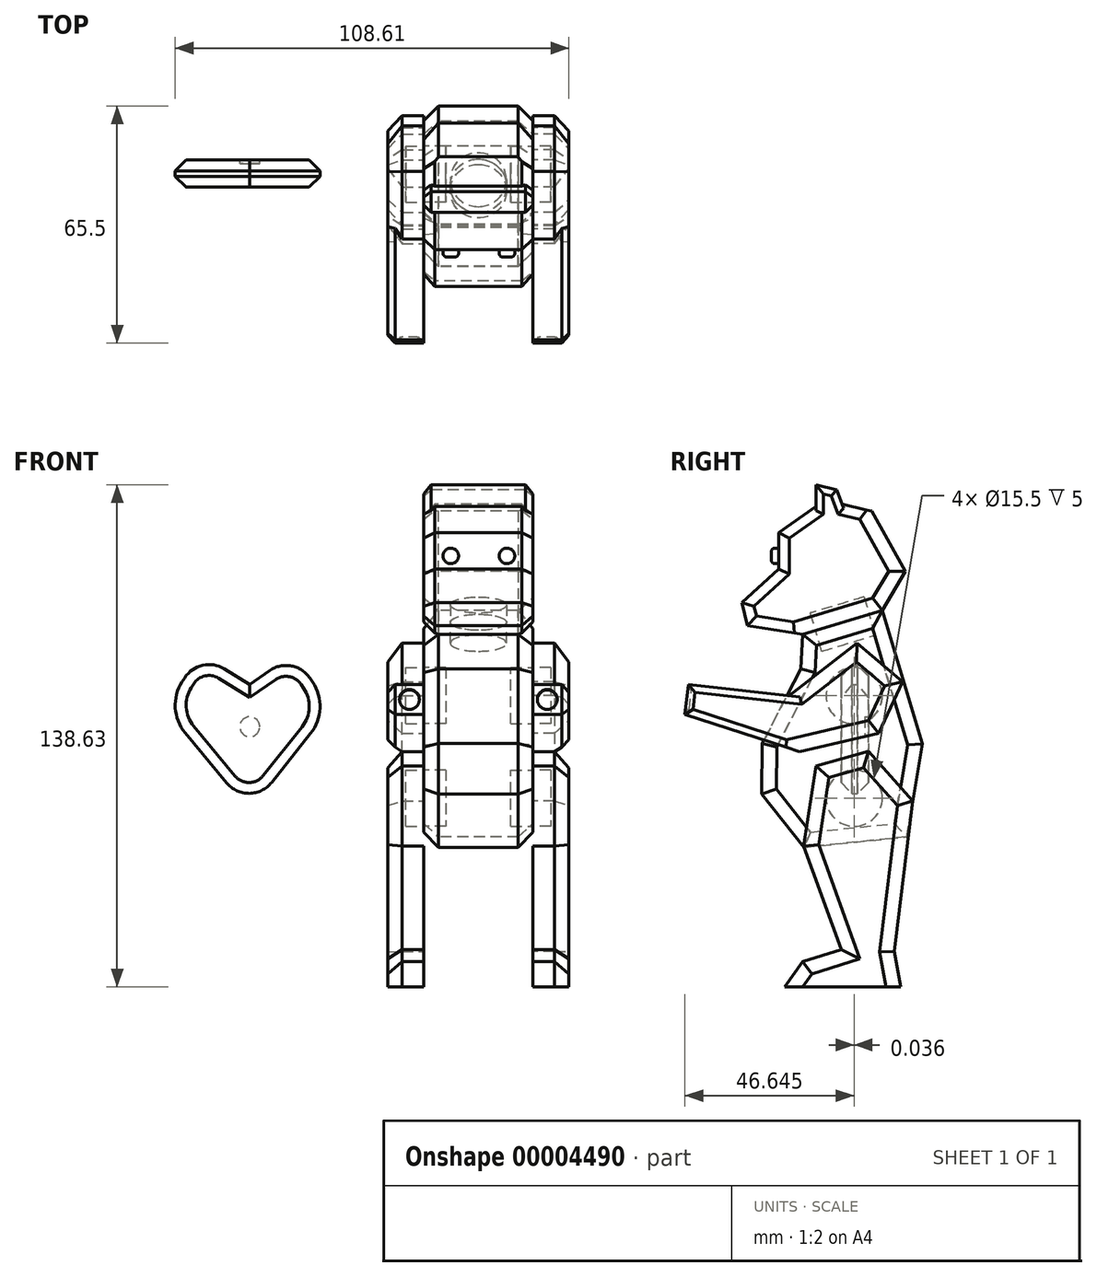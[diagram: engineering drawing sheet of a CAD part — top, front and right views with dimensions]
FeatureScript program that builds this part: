
annotation { "Feature Type Name" : "Feature", "Feature Type Description" : "" }
export const myFeature = defineFeature(function(context is Context, id is Id, definition is map)
    precondition{}
    {
        {
            var Q0;
            Q0=qCreatedBy(makeId("Right.planeOp"),FACE);
            var sketch = newSketch(context, id + "F0", { "sketchPlane" : qUnion([Q0])});
            skLineSegment(sketch, "E0", {"start": v(8.96, -80.35) * mm, "end": v(-23.04, -80.35) * mm});
            skLineSegment(sketch, "E1", {"start": v(-23.04, -80.35) * mm, "end": v(-18.1, -73.4) * mm});
            skLineSegment(sketch, "E2", {"start": v(-18.1, -73.4) * mm, "end": v(-7.52, -70.04) * mm});
            skLineSegment(sketch, "E3", {"start": v(-7.52, -70.04) * mm, "end": v(-17.86, -41.48) * mm});
            skLineSegment(sketch, "E4", {"start": v(-17.86, -41.48) * mm, "end": v(-14.49, -19.35) * mm});
            skLineSegment(sketch, "E5", {"start": v(-14.49, -19.35) * mm, "end": v(0, -15.35) * mm});
            skLineSegment(sketch, "E6", {"start": v(0, -15.35) * mm, "end": v(12.2, -28.97) * mm});
            skLineSegment(sketch, "E7", {"start": v(12.2, -28.97) * mm, "end": v(7.15, -70.52) * mm});
            skLineSegment(sketch, "E8", {"start": v(7.15, -70.52) * mm, "end": v(8.96, -80.35) * mm});
            skCircle(sketch, "E9", {"center": v(-3.9, -28.25) * mm, "radius": 7.75 * mm});
            skSolve(sketch);
        }
        {
            var Q0;
            Q0=qCreatedBy(makeId("Right.planeOp"),FACE);
            var sketch = newSketch(context, id + "F1", { "sketchPlane" : qUnion([Q0])});
            skLineSegment(sketch, "E10", {"start": v(10.62, -38.93) * mm, "end": v(14.91, -13.21) * mm});
            skLineSegment(sketch, "E11", {"start": v(14.91, -13.21) * mm, "end": v(3.82, 23.58) * mm});
            skLineSegment(sketch, "E12", {"start": v(3.82, 23.58) * mm, "end": v(-18.18, 16.97) * mm});
            skLineSegment(sketch, "E13", {"start": v(-18.18, 16.97) * mm, "end": v(-18.65, 7.45) * mm});
            skLineSegment(sketch, "E14", {"start": v(-18.65, 7.45) * mm, "end": v(-29.28, -13.16) * mm});
            skLineSegment(sketch, "E15", {"start": v(-29.28, -13.16) * mm, "end": v(-29.44, -27.12) * mm});
            skLineSegment(sketch, "E16", {"start": v(-29.44, -27.12) * mm, "end": v(-17.76, -41.8) * mm});
            skLineSegment(sketch, "E17", {"start": v(-17.76, -41.8) * mm, "end": v(10.62, -38.93) * mm});
            skLineSegment(sketch, "E18", {"start": v(-3.9, -28.25) * mm, "end": v(-3.9, 9.99) * mm, "construction": true});
            skCircle(sketch, "E19", {"center": v(-3.9, 0) * mm, "radius": 7.75 * mm});
            skCircle(sketch, "E20", {"center": v(-3.9, -28.25) * mm, "radius": 7.75 * mm});
            skSolve(sketch);
        }
        {
            var Q0;
            Q0=qCreatedBy(makeId("Right.planeOp"),FACE);
            var sketch = newSketch(context, id + "F2", { "sketchPlane" : qUnion([Q0])});
            skLineSegment(sketch, "E21", {"start": v(-3.18, 14.54) * mm, "end": v(9.44, 3.85) * mm});
            skLineSegment(sketch, "E22", {"start": v(9.44, 3.85) * mm, "end": v(2.83, -10.31) * mm});
            skLineSegment(sketch, "E23", {"start": v(2.83, -10.31) * mm, "end": v(-19.03, -15.4) * mm});
            skLineSegment(sketch, "E24", {"start": v(-19.03, -15.4) * mm, "end": v(-50.59, -5.17) * mm});
            skLineSegment(sketch, "E25", {"start": v(-50.59, -5.17) * mm, "end": v(-49.66, 3.12) * mm});
            skLineSegment(sketch, "E26", {"start": v(-49.66, 3.12) * mm, "end": v(-21.8, 0) * mm});
            skLineSegment(sketch, "E27", {"start": v(-21.8, 0) * mm, "end": v(-3.18, 14.54) * mm});
            skCircle(sketch, "E28", {"center": v(-3.94, 0) * mm, "radius": 7.75 * mm});
            skSolve(sketch);
        }
        {
            var Q0;
            Q0=qCreatedBy(makeId("Right.planeOp"),FACE);
            var sketch = newSketch(context, id + "F3", { "sketchPlane" : qUnion([Q0])});
            skLineSegment(sketch, "E29", {"start": v(-18.18, 16.97) * mm, "end": v(3.82, 23.58) * mm});
            skLineSegment(sketch, "E30", {"start": v(3.82, 23.58) * mm, "end": v(10.17, 34.3) * mm});
            skLineSegment(sketch, "E31", {"start": v(10.17, 34.3) * mm, "end": v(0.9, 50.93) * mm});
            skLineSegment(sketch, "E32", {"start": v(0.9, 50.93) * mm, "end": v(-7.26, 52.9) * mm});
            skLineSegment(sketch, "E33", {"start": v(-7.26, 52.9) * mm, "end": v(-8.76, 56.87) * mm});
            skLineSegment(sketch, "E34", {"start": v(-8.76, 56.87) * mm, "end": v(-14.44, 58.28) * mm});
            skLineSegment(sketch, "E35", {"start": v(-14.44, 58.28) * mm, "end": v(-14.44, 52.32) * mm});
            skLineSegment(sketch, "E36", {"start": v(-14.44, 52.32) * mm, "end": v(-24.78, 45) * mm});
            skLineSegment(sketch, "E37", {"start": v(-24.78, 45) * mm, "end": v(-24.78, 34.93) * mm});
            skLineSegment(sketch, "E38", {"start": v(-24.78, 34.93) * mm, "end": v(-34.87, 25.75) * mm});
            skLineSegment(sketch, "E39", {"start": v(-34.87, 25.75) * mm, "end": v(-33.35, 19.37) * mm});
            skLineSegment(sketch, "E40", {"start": v(-33.35, 19.37) * mm, "end": v(-18.18, 16.97) * mm});
            skSolve(sketch);
        }
        {
            var Q0;
            Q0=makeQuery(id+"F1.imprint","IMPRINT",FACE,{"disambiguationData":[TD([[makeQuery(id+"F1.imprint","IMPRINT",EDGE,{"derivedFrom":sQuery(id+"F1.wireOp",EDGE,"E10")}),1.0]])]});
            var Q1;
            Q1=makeQuery(id+"F1.imprint","IMPRINT",FACE,{"disambiguationData":[TD([[makeQuery(id+"F1.imprint","IMPRINT",EDGE,{"derivedFrom":sQuery(id+"F1.wireOp",EDGE,"E20")}),1.0]])]});
            var Q2;
            Q2=makeQuery(id+"F1.imprint","IMPRINT",FACE,{"disambiguationData":[TD([[makeQuery(id+"F1.imprint","IMPRINT",EDGE,{"derivedFrom":sQuery(id+"F1.wireOp",EDGE,"E19")}),1.0]])]});
            extrude(context, id + "F4", {"entities" : qUnion([Q0, Q1, Q2]), "depth" : 30 * mm});
        }
        {
            var Q0;
            Q0=makeQuery(id+"F4.opExtrude","CAP_EDGE",EDGE,{"disambiguationData":[OSD([sQuery(id+"F1.wireOp",EDGE,"E15")])],"isStart":false});
            var Q1;
            Q1=makeQuery(id+"F4.opExtrude","CAP_EDGE",EDGE,{"disambiguationData":[OSD([sQuery(id+"F1.wireOp",EDGE,"E14")])],"isStart":false});
            var Q2;
            Q2=makeQuery(id+"F4.opExtrude","CAP_EDGE",EDGE,{"disambiguationData":[OSD([sQuery(id+"F1.wireOp",EDGE,"E13")])],"isStart":false});
            var Q3;
            Q3=makeQuery(id+"F4.opExtrude","CAP_EDGE",EDGE,{"disambiguationData":[OSD([sQuery(id+"F1.wireOp",EDGE,"E12")])],"isStart":false});
            var Q4;
            Q4=makeQuery(id+"F4.opExtrude","CAP_FACE",FACE,{"disambiguationData":[OSD([sQuery(id+"F1.wireOp",EDGE,"E10"),sQuery(id+"F1.wireOp",EDGE,"E11"),sQuery(id+"F1.wireOp",EDGE,"E12"),sQuery(id+"F1.wireOp",EDGE,"E13"),sQuery(id+"F1.wireOp",EDGE,"E14"),sQuery(id+"F1.wireOp",EDGE,"E15"),sQuery(id+"F1.wireOp",EDGE,"E16"),sQuery(id+"F1.wireOp",EDGE,"E17")])],"isStart":false});
            var Q5;
            Q5=makeQuery(id+"F4.opExtrude","CAP_FACE",FACE,{"disambiguationData":[OSD([sQuery(id+"F1.wireOp",EDGE,"E10"),sQuery(id+"F1.wireOp",EDGE,"E11"),sQuery(id+"F1.wireOp",EDGE,"E12"),sQuery(id+"F1.wireOp",EDGE,"E13"),sQuery(id+"F1.wireOp",EDGE,"E14"),sQuery(id+"F1.wireOp",EDGE,"E15"),sQuery(id+"F1.wireOp",EDGE,"E16"),sQuery(id+"F1.wireOp",EDGE,"E17")])],"isStart":true});
            chamfer(context, id + "F5", {"entities" : qUnion([Q0, Q1, Q2, Q3, Q4, Q5]), "width" : 4 * mm, "tangentPropagation" : true});
        }
        {
            var Q0;
            Q0=makeQuery(id+"F4.opExtrude","CAP_FACE",FACE,{"disambiguationData":[OSD([sQuery(id+"F1.wireOp",EDGE,"E10"),sQuery(id+"F1.wireOp",EDGE,"E11"),sQuery(id+"F1.wireOp",EDGE,"E12"),sQuery(id+"F1.wireOp",EDGE,"E13"),sQuery(id+"F1.wireOp",EDGE,"E14"),sQuery(id+"F1.wireOp",EDGE,"E15"),sQuery(id+"F1.wireOp",EDGE,"E16"),sQuery(id+"F1.wireOp",EDGE,"E17")])],"isStart":false});
            var sketch = newSketch(context, id + "F6", { "sketchPlane" : qUnion([Q0])});
            skCircle(sketch, "E41", {"center": v(-3.9, 0) * mm, "radius": 7.75 * mm});
            skCircle(sketch, "E42", {"center": v(-3.9, -28.25) * mm, "radius": 7.75 * mm});
            skSolve(sketch);
        }
        {
            var Q0;
            Q0=makeQuery(id+"F6.imprint","IMPRINT",FACE,{"disambiguationData":[TD([[makeQuery(id+"F6.imprint","IMPRINT",EDGE,{"derivedFrom":sQuery(id+"F6.wireOp",EDGE,"E41")}),1.0]])]});
            var Q1;
            Q1=makeQuery(id+"F6.imprint","IMPRINT",FACE,{"disambiguationData":[TD([[makeQuery(id+"F6.imprint","IMPRINT",EDGE,{"derivedFrom":sQuery(id+"F6.wireOp",EDGE,"E42")}),1.0]])]});
            extrude(context, id + "F7", {"entities" : qUnion([Q0, Q1]), "operationType" : NewBodyOperationType.REMOVE, "oppositeDirection" : true, "depth" : 6 * mm});
        }
        {
            var Q0;
            Q0=makeQuery(id+"F4.opExtrude","CAP_FACE",FACE,{"disambiguationData":[OSD([sQuery(id+"F1.wireOp",EDGE,"E10"),sQuery(id+"F1.wireOp",EDGE,"E11"),sQuery(id+"F1.wireOp",EDGE,"E12"),sQuery(id+"F1.wireOp",EDGE,"E13"),sQuery(id+"F1.wireOp",EDGE,"E14"),sQuery(id+"F1.wireOp",EDGE,"E15"),sQuery(id+"F1.wireOp",EDGE,"E16"),sQuery(id+"F1.wireOp",EDGE,"E17")])],"isStart":false});
            var Q1;
            Q1=makeQuery(id+"F4.opExtrude","CAP_FACE",FACE,{"disambiguationData":[OSD([sQuery(id+"F1.wireOp",EDGE,"E10"),sQuery(id+"F1.wireOp",EDGE,"E11"),sQuery(id+"F1.wireOp",EDGE,"E12"),sQuery(id+"F1.wireOp",EDGE,"E13"),sQuery(id+"F1.wireOp",EDGE,"E14"),sQuery(id+"F1.wireOp",EDGE,"E15"),sQuery(id+"F1.wireOp",EDGE,"E16"),sQuery(id+"F1.wireOp",EDGE,"E17")])],"isStart":true});
            cPlane(context, id + "F8", {"entities" : qUnion([Q0, Q1]), "cplaneType" : CPlaneType.MID_PLANE, "offset" : 150 * mm, "width" : 150 * mm, "height" : 150 * mm});
        }
        {
            var Q0;
            Q0=makeQuery(id+"F4.opExtrude","CAP_FACE",FACE,{"disambiguationData":[OSD([sQuery(id+"F1.wireOp",EDGE,"E10"),sQuery(id+"F1.wireOp",EDGE,"E11"),sQuery(id+"F1.wireOp",EDGE,"E12"),sQuery(id+"F1.wireOp",EDGE,"E13"),sQuery(id+"F1.wireOp",EDGE,"E14"),sQuery(id+"F1.wireOp",EDGE,"E15"),sQuery(id+"F1.wireOp",EDGE,"E16"),sQuery(id+"F1.wireOp",EDGE,"E17")])],"isStart":true});
            var sketch = newSketch(context, id + "F9", { "sketchPlane" : qUnion([Q0])});
            skCircle(sketch, "E43", {"center": v(3.9, -28.25) * mm, "radius": 7.75 * mm});
            skCircle(sketch, "E44", {"center": v(3.9, 0) * mm, "radius": 7.75 * mm});
            skSolve(sketch);
        }
        {
            var Q0;
            Q0=makeQuery(id+"F9.imprint","IMPRINT",FACE,{"disambiguationData":[TD([[makeQuery(id+"F9.imprint","IMPRINT",EDGE,{"derivedFrom":sQuery(id+"F9.wireOp",EDGE,"E44")}),1.0]])]});
            var Q1;
            Q1=makeQuery(id+"F9.imprint","IMPRINT",FACE,{"disambiguationData":[TD([[makeQuery(id+"F9.imprint","IMPRINT",EDGE,{"derivedFrom":sQuery(id+"F9.wireOp",EDGE,"E43")}),1.0]])]});
            extrude(context, id + "F10", {"entities" : qUnion([Q0, Q1]), "operationType" : NewBodyOperationType.REMOVE, "oppositeDirection" : true, "depth" : 6 * mm});
        }
        {
            var Q0;
            Q0=makeQuery(id+"F4.opExtrude","SWEPT_FACE",FACE,{"disambiguationData":[OSD([sQuery(id+"F1.wireOp",EDGE,"E12")])]});
            var sketch = newSketch(context, id + "F11", { "sketchPlane" : qUnion([Q0])});
            skLineSegment(sketch, "E45", {"start": v(4, 10.45) * mm, "end": v(26, -12.53) * mm, "construction": true});
            skLineSegment(sketch, "E46", {"start": v(4, -12.53) * mm, "end": v(26, 10.45) * mm, "construction": true});
            skCircle(sketch, "E47", {"center": v(15, -1.04) * mm, "radius": 7.75 * mm});
            skSolve(sketch);
        }
        {
            var Q0;
            Q0=makeQuery(id+"F11.imprint","IMPRINT",FACE,{"disambiguationData":[TD([[makeQuery(id+"F11.imprint","IMPRINT",EDGE,{"derivedFrom":sQuery(id+"F11.wireOp",EDGE,"E47")}),1.0]])]});
            extrude(context, id + "F12", {"entities" : qUnion([Q0]), "operationType" : NewBodyOperationType.REMOVE, "oppositeDirection" : true, "depth" : 6 * mm});
        }
        {
            var Q0;
            Q0=makeQuery(id+"F3.imprint","IMPRINT",FACE,{"disambiguationData":[TD([[makeQuery(id+"F3.imprint","IMPRINT",EDGE,{"derivedFrom":sQuery(id+"F3.wireOp",EDGE,"E29")}),1.0]])]});
            extrude(context, id + "F13", {"entities" : qUnion([Q0]), "depth" : 30 * mm});
        }
        {
            var Q0;
            Q0=makeQuery(id+"F13.opExtrude","CAP_EDGE",EDGE,{"disambiguationData":[OSD([sQuery(id+"F3.wireOp",EDGE,"E29")])],"isStart":false});
            var Q1;
            Q1=makeQuery(id+"F13.opExtrude","CAP_EDGE",EDGE,{"disambiguationData":[OSD([sQuery(id+"F3.wireOp",EDGE,"E29")])],"isStart":true});
            var Q2;
            Q2=makeQuery(id+"F13.opExtrude","CAP_EDGE",EDGE,{"disambiguationData":[OSD([sQuery(id+"F3.wireOp",EDGE,"E30")])],"isStart":false});
            var Q3;
            Q3=makeQuery(id+"F13.opExtrude","CAP_EDGE",EDGE,{"disambiguationData":[OSD([sQuery(id+"F3.wireOp",EDGE,"E31")])],"isStart":false});
            var Q4;
            Q4=makeQuery(id+"F13.opExtrude","CAP_EDGE",EDGE,{"disambiguationData":[OSD([sQuery(id+"F3.wireOp",EDGE,"E30")])],"isStart":true});
            var Q5;
            Q5=makeQuery(id+"F13.opExtrude","CAP_EDGE",EDGE,{"disambiguationData":[OSD([sQuery(id+"F3.wireOp",EDGE,"E31")])],"isStart":true});
            chamfer(context, id + "F14", {"entities" : qUnion([Q0, Q1, Q2, Q3, Q4, Q5]), "width" : 4 * mm, "tangentPropagation" : true});
        }
        {
            var Q0;
            Q0=makeQuery(id+"F13.opExtrude","CAP_EDGE",EDGE,{"disambiguationData":[OSD([sQuery(id+"F3.wireOp",EDGE,"E40")])],"isStart":false});
            var Q1;
            Q1=makeQuery(id+"F13.opExtrude","CAP_EDGE",EDGE,{"disambiguationData":[OSD([sQuery(id+"F3.wireOp",EDGE,"E39")])],"isStart":false});
            var Q2;
            Q2=makeQuery(id+"F13.opExtrude","CAP_EDGE",EDGE,{"disambiguationData":[OSD([sQuery(id+"F3.wireOp",EDGE,"E38")])],"isStart":false});
            var Q3;
            Q3=makeQuery(id+"F13.opExtrude","CAP_EDGE",EDGE,{"disambiguationData":[OSD([sQuery(id+"F3.wireOp",EDGE,"E37")])],"isStart":false});
            var Q4;
            Q4=makeQuery(id+"F13.opExtrude","CAP_EDGE",EDGE,{"disambiguationData":[OSD([sQuery(id+"F3.wireOp",EDGE,"E36")])],"isStart":false});
            var Q5;
            Q5=makeQuery(id+"F13.opExtrude","CAP_EDGE",EDGE,{"disambiguationData":[OSD([sQuery(id+"F3.wireOp",EDGE,"E32")])],"isStart":false});
            var Q6;
            Q6=makeQuery(id+"F13.opExtrude","CAP_EDGE",EDGE,{"disambiguationData":[OSD([sQuery(id+"F3.wireOp",EDGE,"E32")])],"isStart":true});
            var Q7;
            Q7=makeQuery(id+"F13.opExtrude","CAP_EDGE",EDGE,{"disambiguationData":[OSD([sQuery(id+"F3.wireOp",EDGE,"E36")])],"isStart":true});
            var Q8;
            Q8=makeQuery(id+"F13.opExtrude","CAP_EDGE",EDGE,{"disambiguationData":[OSD([sQuery(id+"F3.wireOp",EDGE,"E37")])],"isStart":true});
            var Q9;
            Q9=makeQuery(id+"F13.opExtrude","CAP_EDGE",EDGE,{"disambiguationData":[OSD([sQuery(id+"F3.wireOp",EDGE,"E38")])],"isStart":true});
            var Q10;
            Q10=makeQuery(id+"F13.opExtrude","CAP_EDGE",EDGE,{"disambiguationData":[OSD([sQuery(id+"F3.wireOp",EDGE,"E39")])],"isStart":true});
            var Q11;
            Q11=makeQuery(id+"F13.opExtrude","CAP_EDGE",EDGE,{"disambiguationData":[OSD([sQuery(id+"F3.wireOp",EDGE,"E40")])],"isStart":true});
            chamfer(context, id + "F15", {"entities" : qUnion([Q0, Q1, Q2, Q3, Q4, Q5, Q6, Q7, Q8, Q9, Q10, Q11]), "width" : 3 * mm, "tangentPropagation" : true});
        }
        {
            var Q0;
            Q0=makeQuery(id+"F13.opExtrude","CAP_EDGE",EDGE,{"disambiguationData":[OSD([sQuery(id+"F3.wireOp",EDGE,"E35")])],"isStart":false});
            var Q1;
            Q1=makeQuery(id+"F13.opExtrude","CAP_EDGE",EDGE,{"disambiguationData":[OSD([sQuery(id+"F3.wireOp",EDGE,"E33")])],"isStart":false});
            var Q2;
            Q2=makeQuery(id+"F13.opExtrude","CAP_EDGE",EDGE,{"disambiguationData":[OSD([sQuery(id+"F3.wireOp",EDGE,"E34")])],"isStart":false});
            var Q3;
            Q3=makeQuery(id+"F13.opExtrude","CAP_EDGE",EDGE,{"disambiguationData":[OSD([sQuery(id+"F3.wireOp",EDGE,"E33")])],"isStart":true});
            var Q4;
            Q4=makeQuery(id+"F13.opExtrude","CAP_EDGE",EDGE,{"disambiguationData":[OSD([sQuery(id+"F3.wireOp",EDGE,"E35")])],"isStart":true});
            var Q5;
            Q5=makeQuery(id+"F13.opExtrude","CAP_EDGE",EDGE,{"disambiguationData":[OSD([sQuery(id+"F3.wireOp",EDGE,"E34")])],"isStart":true});
            chamfer(context, id + "F16", {"entities" : qUnion([Q0, Q1, Q2, Q3, Q4, Q5]), "width" : 2 * mm, "tangentPropagation" : true});
        }
        {
            var Q0;
            Q0=makeQuery(id+"F2.imprint","IMPRINT",FACE,{"disambiguationData":[TD([[makeQuery(id+"F2.imprint","IMPRINT",EDGE,{"derivedFrom":sQuery(id+"F2.wireOp",EDGE,"E21")}),-1.0]])]});
            var Q1;
            Q1=makeQuery(id+"F2.imprint","IMPRINT",FACE,{"disambiguationData":[TD([[makeQuery(id+"F2.imprint","IMPRINT",EDGE,{"derivedFrom":sQuery(id+"F2.wireOp",EDGE,"E28")}),1.0]])]});
            extrude(context, id + "F17", {"entities" : qUnion([Q0, Q1]), "oppositeDirection" : true, "depth" : 10 * mm});
        }
        {
            var Q0;
            Q0=makeQuery(id+"F13.opExtrude","SWEPT_FACE",FACE,{"disambiguationData":[OSD([sQuery(id+"F3.wireOp",EDGE,"E29")])]});
            var sketch = newSketch(context, id + "F18", { "sketchPlane" : qUnion([Q0])});
            skLineSegment(sketch, "E48", {"start": v(26, -10.44) * mm, "end": v(4, 12.52) * mm, "construction": true});
            skLineSegment(sketch, "E49", {"start": v(26, 12.52) * mm, "end": v(4, -10.44) * mm, "construction": true});
            skCircle(sketch, "E50", {"center": v(15, 1.04) * mm, "radius": 7.75 * mm});
            skSolve(sketch);
        }
        {
            var Q0;
            Q0=makeQuery(id+"F18.imprint","IMPRINT",FACE,{"disambiguationData":[TD([[makeQuery(id+"F18.imprint","IMPRINT",EDGE,{"derivedFrom":sQuery(id+"F18.wireOp",EDGE,"E50")}),1.0]])]});
            extrude(context, id + "F19", {"entities" : qUnion([Q0]), "operationType" : NewBodyOperationType.REMOVE, "oppositeDirection" : true, "depth" : 5 * mm});
        }
        {
            var Q0;
            Q0=makeQuery(id+"F2.imprint","IMPRINT",FACE,{"disambiguationData":[TD([[makeQuery(id+"F2.imprint","IMPRINT",EDGE,{"derivedFrom":sQuery(id+"F2.wireOp",EDGE,"E21")}),-1.0]])]});
            var sketch = newSketch(context, id + "F20", { "sketchPlane" : qUnion([Q0])});
            skCircle(sketch, "E51", {"center": v(-3.94, 0) * mm, "radius": 7.75 * mm});
            skSolve(sketch);
        }
        {
            var Q0;
            Q0=makeQuery(id+"F17.opExtrude","SWEPT_BODY",BODY,{"disambiguationData":[OSD([sQuery(id+"F2.wireOp",EDGE,"E21"),sQuery(id+"F2.wireOp",EDGE,"E22"),sQuery(id+"F2.wireOp",EDGE,"E23"),sQuery(id+"F2.wireOp",EDGE,"E24"),sQuery(id+"F2.wireOp",EDGE,"E25"),sQuery(id+"F2.wireOp",EDGE,"E26"),sQuery(id+"F2.wireOp",EDGE,"E27")])]});
            var Q1;
            Q1=qCreatedBy(id+"F8.planeOp",FACE);
            mirror(context, id + "F21", {"entities" : qUnion([Q0]), "mirrorPlane" : qUnion([Q1])});
        }
        {
            var Q0;
            Q0=makeQuery(id+"F0.imprint","IMPRINT",FACE,{"disambiguationData":[TD([[makeQuery(id+"F0.imprint","IMPRINT",EDGE,{"derivedFrom":sQuery(id+"F0.wireOp",EDGE,"E0")}),-1.0]])]});
            var Q1;
            Q1=makeQuery(id+"F0.imprint","IMPRINT",FACE,{"disambiguationData":[TD([[makeQuery(id+"F0.imprint","IMPRINT",EDGE,{"derivedFrom":sQuery(id+"F0.wireOp",EDGE,"E9")}),1.0]])]});
            extrude(context, id + "F22", {"entities" : qUnion([Q0, Q1]), "oppositeDirection" : true, "depth" : 10 * mm});
        }
        {
            var Q0;
            Q0=makeQuery(id+"F22.opExtrude","SWEPT_BODY",BODY,{"disambiguationData":[OSD([sQuery(id+"F0.wireOp",EDGE,"E0"),sQuery(id+"F0.wireOp",EDGE,"E1"),sQuery(id+"F0.wireOp",EDGE,"E2"),sQuery(id+"F0.wireOp",EDGE,"E3"),sQuery(id+"F0.wireOp",EDGE,"E4"),sQuery(id+"F0.wireOp",EDGE,"E5"),sQuery(id+"F0.wireOp",EDGE,"E6"),sQuery(id+"F0.wireOp",EDGE,"E7"),sQuery(id+"F0.wireOp",EDGE,"E8")])]});
            var Q1;
            Q1=qCreatedBy(id+"F8.planeOp",FACE);
            mirror(context, id + "F23", {"entities" : qUnion([Q0]), "mirrorPlane" : qUnion([Q1])});
        }
        {
            var Q0;
            Q0=makeQuery(id+"F22.opExtrude","CAP_EDGE",EDGE,{"disambiguationData":[OSD([sQuery(id+"F0.wireOp",EDGE,"E6")])],"isStart":false});
            var Q1;
            Q1=makeQuery(id+"F22.opExtrude","CAP_EDGE",EDGE,{"disambiguationData":[OSD([sQuery(id+"F0.wireOp",EDGE,"E5")])],"isStart":false});
            var Q2;
            Q2=makeQuery(id+"F22.opExtrude","CAP_EDGE",EDGE,{"disambiguationData":[OSD([sQuery(id+"F0.wireOp",EDGE,"E4")])],"isStart":false});
            var Q3;
            Q3=makeQuery(id+"F22.opExtrude","CAP_EDGE",EDGE,{"disambiguationData":[OSD([sQuery(id+"F0.wireOp",EDGE,"E3")])],"isStart":false});
            var Q4;
            Q4=makeQuery(id+"F22.opExtrude","CAP_EDGE",EDGE,{"disambiguationData":[OSD([sQuery(id+"F0.wireOp",EDGE,"E7")])],"isStart":false});
            var Q5;
            Q5=makeQuery(id+"F23.opPattern","COPY",EDGE,{"derivedFrom":makeQuery(id+"F22.opExtrude","CAP_EDGE",EDGE,{"disambiguationData":[OSD([sQuery(id+"F0.wireOp",EDGE,"E5")])],"isStart":false}),"instanceName":"1"});
            var Q6;
            Q6=makeQuery(id+"F23.opPattern","COPY",EDGE,{"derivedFrom":makeQuery(id+"F22.opExtrude","CAP_EDGE",EDGE,{"disambiguationData":[OSD([sQuery(id+"F0.wireOp",EDGE,"E6")])],"isStart":false}),"instanceName":"1"});
            var Q7;
            Q7=makeQuery(id+"F23.opPattern","COPY",EDGE,{"derivedFrom":makeQuery(id+"F22.opExtrude","CAP_EDGE",EDGE,{"disambiguationData":[OSD([sQuery(id+"F0.wireOp",EDGE,"E4")])],"isStart":false}),"instanceName":"1"});
            var Q8;
            Q8=makeQuery(id+"F23.opPattern","COPY",EDGE,{"derivedFrom":makeQuery(id+"F22.opExtrude","CAP_EDGE",EDGE,{"disambiguationData":[OSD([sQuery(id+"F0.wireOp",EDGE,"E3")])],"isStart":false}),"instanceName":"1"});
            var Q9;
            Q9=makeQuery(id+"F23.opPattern","COPY",EDGE,{"derivedFrom":makeQuery(id+"F22.opExtrude","CAP_EDGE",EDGE,{"disambiguationData":[OSD([sQuery(id+"F0.wireOp",EDGE,"E7")])],"isStart":false}),"instanceName":"1"});
            var Q10;
            Q10=makeQuery(id+"F22.opExtrude","CAP_EDGE",EDGE,{"disambiguationData":[OSD([sQuery(id+"F0.wireOp",EDGE,"E8")])],"isStart":false});
            var Q11;
            Q11=makeQuery(id+"F23.opPattern","COPY",EDGE,{"derivedFrom":makeQuery(id+"F22.opExtrude","CAP_EDGE",EDGE,{"disambiguationData":[OSD([sQuery(id+"F0.wireOp",EDGE,"E8")])],"isStart":false}),"instanceName":"1"});
            var Q12;
            Q12=makeQuery(id+"F23.opPattern","COPY",EDGE,{"derivedFrom":makeQuery(id+"F22.opExtrude","CAP_EDGE",EDGE,{"disambiguationData":[OSD([sQuery(id+"F0.wireOp",EDGE,"E2")])],"isStart":false}),"instanceName":"1"});
            var Q13;
            Q13=makeQuery(id+"F23.opPattern","COPY",EDGE,{"derivedFrom":makeQuery(id+"F22.opExtrude","CAP_EDGE",EDGE,{"disambiguationData":[OSD([sQuery(id+"F0.wireOp",EDGE,"E1")])],"isStart":false}),"instanceName":"1"});
            var Q14;
            Q14=makeQuery(id+"F22.opExtrude","CAP_EDGE",EDGE,{"disambiguationData":[OSD([sQuery(id+"F0.wireOp",EDGE,"E2")])],"isStart":false});
            var Q15;
            Q15=makeQuery(id+"F22.opExtrude","CAP_EDGE",EDGE,{"disambiguationData":[OSD([sQuery(id+"F0.wireOp",EDGE,"E1")])],"isStart":false});
            chamfer(context, id + "F24", {"entities" : qUnion([Q0, Q1, Q2, Q3, Q4, Q5, Q6, Q7, Q8, Q9, Q10, Q11, Q12, Q13, Q14, Q15]), "width" : 4 * mm, "tangentPropagation" : true});
        }
        {
            var Q0;
            Q0=makeQuery(id+"F21.opPattern","COPY",EDGE,{"derivedFrom":makeQuery(id+"F17.opExtrude","CAP_EDGE",EDGE,{"disambiguationData":[OSD([sQuery(id+"F2.wireOp",EDGE,"E27")])],"isStart":false}),"instanceName":"1"});
            var Q1;
            Q1=makeQuery(id+"F21.opPattern","COPY",EDGE,{"derivedFrom":makeQuery(id+"F17.opExtrude","CAP_EDGE",EDGE,{"disambiguationData":[OSD([sQuery(id+"F2.wireOp",EDGE,"E21")])],"isStart":false}),"instanceName":"1"});
            var Q2;
            Q2=makeQuery(id+"F21.opPattern","COPY",EDGE,{"derivedFrom":makeQuery(id+"F17.opExtrude","CAP_EDGE",EDGE,{"disambiguationData":[OSD([sQuery(id+"F2.wireOp",EDGE,"E22")])],"isStart":false}),"instanceName":"1"});
            var Q3;
            Q3=makeQuery(id+"F21.opPattern","COPY",EDGE,{"derivedFrom":makeQuery(id+"F17.opExtrude","CAP_EDGE",EDGE,{"disambiguationData":[OSD([sQuery(id+"F2.wireOp",EDGE,"E23")])],"isStart":false}),"instanceName":"1"});
            var Q4;
            Q4=makeQuery(id+"F17.opExtrude","CAP_EDGE",EDGE,{"disambiguationData":[OSD([sQuery(id+"F2.wireOp",EDGE,"E27")])],"isStart":false});
            var Q5;
            Q5=makeQuery(id+"F17.opExtrude","CAP_EDGE",EDGE,{"disambiguationData":[OSD([sQuery(id+"F2.wireOp",EDGE,"E21")])],"isStart":false});
            var Q6;
            Q6=makeQuery(id+"F17.opExtrude","CAP_EDGE",EDGE,{"disambiguationData":[OSD([sQuery(id+"F2.wireOp",EDGE,"E22")])],"isStart":false});
            var Q7;
            Q7=makeQuery(id+"F17.opExtrude","CAP_EDGE",EDGE,{"disambiguationData":[OSD([sQuery(id+"F2.wireOp",EDGE,"E23")])],"isStart":false});
            chamfer(context, id + "F25", {"entities" : qUnion([Q0, Q1, Q2, Q3, Q4, Q5, Q6, Q7]), "width" : 4 * mm, "tangentPropagation" : true});
        }
        {
            var Q0;
            Q0=makeQuery(id+"F17.opExtrude","CAP_EDGE",EDGE,{"disambiguationData":[OSD([sQuery(id+"F2.wireOp",EDGE,"E26")])],"isStart":false});
            var Q1;
            Q1=makeQuery(id+"F17.opExtrude","CAP_EDGE",EDGE,{"disambiguationData":[OSD([sQuery(id+"F2.wireOp",EDGE,"E24")])],"isStart":false});
            var Q2;
            Q2=makeQuery(id+"F21.opPattern","COPY",EDGE,{"derivedFrom":makeQuery(id+"F17.opExtrude","CAP_EDGE",EDGE,{"disambiguationData":[OSD([sQuery(id+"F2.wireOp",EDGE,"E26")])],"isStart":false}),"instanceName":"1"});
            var Q3;
            Q3=makeQuery(id+"F21.opPattern","COPY",EDGE,{"derivedFrom":makeQuery(id+"F17.opExtrude","CAP_EDGE",EDGE,{"disambiguationData":[OSD([sQuery(id+"F2.wireOp",EDGE,"E24")])],"isStart":false}),"instanceName":"1"});
            var Q4;
            Q4=makeQuery(id+"F21.opPattern","COPY",EDGE,{"derivedFrom":makeQuery(id+"F17.opExtrude","CAP_EDGE",EDGE,{"disambiguationData":[OSD([sQuery(id+"F2.wireOp",EDGE,"E25")])],"isStart":false}),"instanceName":"1"});
            var Q5;
            Q5=makeQuery(id+"F17.opExtrude","CAP_EDGE",EDGE,{"disambiguationData":[OSD([sQuery(id+"F2.wireOp",EDGE,"E25")])],"isStart":false});
            chamfer(context, id + "F26", {"entities" : qUnion([Q0, Q1, Q2, Q3, Q4, Q5]), "width" : 2 * mm, "tangentPropagation" : true});
        }
        {
            var Q0;
            Q0=makeQuery(id+"F0.imprint","IMPRINT",FACE,{"disambiguationData":[TD([[makeQuery(id+"F0.imprint","IMPRINT",EDGE,{"derivedFrom":sQuery(id+"F0.wireOp",EDGE,"E9")}),1.0]])]});
            extrude(context, id + "F27", {"entities" : qUnion([Q0]), "operationType" : NewBodyOperationType.REMOVE, "oppositeDirection" : true, "depth" : 5 * mm});
        }
        {
            var Q0;
            Q0=makeQuery(id+"F20.imprint","IMPRINT",FACE,{"disambiguationData":[TD([[makeQuery(id+"F20.imprint","IMPRINT",EDGE,{"derivedFrom":sQuery(id+"F20.wireOp",EDGE,"E51")}),1.0]])]});
            extrude(context, id + "F28", {"entities" : qUnion([Q0]), "operationType" : NewBodyOperationType.REMOVE, "oppositeDirection" : true, "depth" : 5 * mm});
        }
        {
            var Q0;
            Q0=makeQuery(id+"F23.opPattern","COPY",FACE,{"derivedFrom":makeQuery(id+"F22.opExtrude","CAP_FACE",FACE,{"disambiguationData":[OSD([sQuery(id+"F0.wireOp",EDGE,"E0"),sQuery(id+"F0.wireOp",EDGE,"E1"),sQuery(id+"F0.wireOp",EDGE,"E2"),sQuery(id+"F0.wireOp",EDGE,"E3"),sQuery(id+"F0.wireOp",EDGE,"E4"),sQuery(id+"F0.wireOp",EDGE,"E5"),sQuery(id+"F0.wireOp",EDGE,"E6"),sQuery(id+"F0.wireOp",EDGE,"E7"),sQuery(id+"F0.wireOp",EDGE,"E8")])],"isStart":true}),"instanceName":"1"});
            var sketch = newSketch(context, id + "F29", { "sketchPlane" : qUnion([Q0])});
            skCircle(sketch, "E52", {"center": v(3.9, -28.25) * mm, "radius": 7.75 * mm});
            skSolve(sketch);
        }
        {
            var Q0;
            Q0=makeQuery(id+"F29.imprint","IMPRINT",FACE,{"disambiguationData":[TD([[makeQuery(id+"F29.imprint","IMPRINT",EDGE,{"derivedFrom":sQuery(id+"F29.wireOp",EDGE,"E52")}),1.0]])]});
            extrude(context, id + "F30", {"entities" : qUnion([Q0]), "operationType" : NewBodyOperationType.REMOVE, "oppositeDirection" : true, "depth" : 5 * mm});
        }
        {
            var Q0;
            Q0=makeQuery(id+"F21.opPattern","COPY",FACE,{"derivedFrom":makeQuery(id+"F17.opExtrude","CAP_FACE",FACE,{"disambiguationData":[OSD([sQuery(id+"F2.wireOp",EDGE,"E21"),sQuery(id+"F2.wireOp",EDGE,"E22"),sQuery(id+"F2.wireOp",EDGE,"E23"),sQuery(id+"F2.wireOp",EDGE,"E24"),sQuery(id+"F2.wireOp",EDGE,"E25"),sQuery(id+"F2.wireOp",EDGE,"E26"),sQuery(id+"F2.wireOp",EDGE,"E27")])],"isStart":true}),"instanceName":"1"});
            var sketch = newSketch(context, id + "F31", { "sketchPlane" : qUnion([Q0])});
            skCircle(sketch, "E53", {"center": v(3.94, 0) * mm, "radius": 7.75 * mm});
            skSolve(sketch);
        }
        {
            var Q0;
            Q0=makeQuery(id+"F31.imprint","IMPRINT",FACE,{"disambiguationData":[TD([[makeQuery(id+"F31.imprint","IMPRINT",EDGE,{"derivedFrom":sQuery(id+"F31.wireOp",EDGE,"E53")}),1.0]])]});
            extrude(context, id + "F32", {"entities" : qUnion([Q0]), "operationType" : NewBodyOperationType.REMOVE, "oppositeDirection" : true, "depth" : 5 * mm});
        }
        {
            var Q0;
            Q0=makeQuery(id+"F17.opExtrude","SWEPT_FACE",FACE,{"disambiguationData":[OSD([sQuery(id+"F2.wireOp",EDGE,"E25")])]});
            var sketch = newSketch(context, id + "F33", { "sketchPlane" : qUnion([Q0])});
            skLineSegment(sketch, "E54", {"start": v(-8, -2.43) * mm, "end": v(0, -10.77) * mm, "construction": true});
            skLineSegment(sketch, "E55", {"start": v(-8, -10.77) * mm, "end": v(0, -2.43) * mm, "construction": true});
            skCircle(sketch, "E56", {"center": v(-4, -6.6) * mm, "radius": 2.75 * mm});
            skSolve(sketch);
        }
        {
            var Q0;
            Q0=makeQuery(id+"F33.imprint","IMPRINT",FACE,{"disambiguationData":[TD([[makeQuery(id+"F33.imprint","IMPRINT",EDGE,{"derivedFrom":sQuery(id+"F33.wireOp",EDGE,"E56")}),1.0]])]});
            extrude(context, id + "F34", {"entities" : qUnion([Q0]), "operationType" : NewBodyOperationType.REMOVE, "oppositeDirection" : true, "depth" : 1 * mm});
        }
        {
            var Q0;
            Q0=makeQuery(id+"F21.opPattern","COPY",FACE,{"derivedFrom":makeQuery(id+"F17.opExtrude","SWEPT_FACE",FACE,{"disambiguationData":[OSD([sQuery(id+"F2.wireOp",EDGE,"E25")])]}),"instanceName":"1"});
            var sketch = newSketch(context, id + "F35", { "sketchPlane" : qUnion([Q0])});
            skLineSegment(sketch, "E57", {"start": v(30, -2.43) * mm, "end": v(38, -10.77) * mm, "construction": true});
            skLineSegment(sketch, "E58", {"start": v(30, -10.77) * mm, "end": v(38, -2.43) * mm, "construction": true});
            skCircle(sketch, "E59", {"center": v(34, -6.6) * mm, "radius": 2.75 * mm});
            skSolve(sketch);
        }
        {
            var Q0;
            Q0=makeQuery(id+"F35.imprint","IMPRINT",FACE,{"disambiguationData":[TD([[makeQuery(id+"F35.imprint","IMPRINT",EDGE,{"derivedFrom":sQuery(id+"F35.wireOp",EDGE,"E59")}),1.0]])]});
            extrude(context, id + "F36", {"entities" : qUnion([Q0]), "operationType" : NewBodyOperationType.REMOVE, "oppositeDirection" : true, "depth" : 1 * mm});
        }
        {
            var Q0;
            Q0=makeQuery(id+"F13.opExtrude","SWEPT_FACE",FACE,{"disambiguationData":[OSD([sQuery(id+"F3.wireOp",EDGE,"E37")])]});
            var sketch = newSketch(context, id + "F37", { "sketchPlane" : qUnion([Q0])});
            skLineSegment(sketch, "E60", {"start": v(4.61, 38.6) * mm, "end": v(25.95, 38.6) * mm, "construction": true});
            skCircle(sketch, "E61", {"center": v(7.41, 38.6) * mm, "radius": 2.14 * mm});
            skCircle(sketch, "E62", {"center": v(22.9, 38.6) * mm, "radius": 2.14 * mm});
            skSolve(sketch);
        }
        {
            var Q0;
            Q0=makeQuery(id+"F37.imprint","IMPRINT",FACE,{"disambiguationData":[TD([[makeQuery(id+"F37.imprint","IMPRINT",EDGE,{"derivedFrom":sQuery(id+"F37.wireOp",EDGE,"E61")}),1.0]])]});
            var Q1;
            Q1=makeQuery(id+"F37.imprint","IMPRINT",FACE,{"disambiguationData":[TD([[makeQuery(id+"F37.imprint","IMPRINT",EDGE,{"derivedFrom":sQuery(id+"F37.wireOp",EDGE,"E62")}),1.0]])]});
            extrude(context, id + "F38", {"entities" : qUnion([Q0, Q1]), "operationType" : NewBodyOperationType.ADD, "depth" : 2 * mm});
        }
        {
            var Q0;
            Q0=makeQuery(id+"F38.opExtrude","CAP_EDGE",EDGE,{"disambiguationData":[OSD([sQuery(id+"F37.wireOp",EDGE,"E62")])],"isStart":false});
            var Q1;
            Q1=makeQuery(id+"F38.opExtrude","CAP_EDGE",EDGE,{"disambiguationData":[OSD([sQuery(id+"F37.wireOp",EDGE,"E61")])],"isStart":false});
            fillet(context, id + "F39", {"entities" : qUnion([Q0, Q1]), "radius" : 1 * mm, "tangentPropagation" : true, "allowEdgeOverflow" : false});
        }
        {
            var Q0;
            Q0=qCreatedBy(makeId("Front.planeOp"),FACE);
            var sketch = newSketch(context, id + "F40", { "sketchPlane" : qUnion([Q0])});
            skLineSegment(sketch, "E63", {"start": v(-48.13, -31.62) * mm, "end": v(-71.45, -3.52) * mm});
            skLineSegment(sketch, "E64", {"start": v(-71.45, -3.52) * mm, "end": v(-61.77, 11.54) * mm});
            skLineSegment(sketch, "E65", {"start": v(-61.77, 11.54) * mm, "end": v(-48.13, 3.15) * mm});
            skLineSegment(sketch, "E66", {"start": v(-48.13, 3.15) * mm, "end": v(-35.91, 11.54) * mm});
            skLineSegment(sketch, "E67", {"start": v(-35.91, 11.54) * mm, "end": v(-25.8, -3.52) * mm});
            skLineSegment(sketch, "E68", {"start": v(-25.8, -3.52) * mm, "end": v(-48.13, -31.62) * mm});
            skSolve(sketch);
        }
        {
            var Q0;
            Q0=makeQuery(id+"F40.imprint","IMPRINT",FACE,{"disambiguationData":[TD([[makeQuery(id+"F40.imprint","IMPRINT",EDGE,{"derivedFrom":sQuery(id+"F40.wireOp",EDGE,"E63")}),-1.0]])]});
            extrude(context, id + "F41", {"entities" : qUnion([Q0]), "depth" : 7.5 * mm});
        }
        {
            var Q0;
            Q0=makeQuery(id+"F41.opExtrude","SWEPT_EDGE",EDGE,{"disambiguationData":[OSD([sQuery(id+"F40.wireOp",EDGE,"E66"),sQuery(id+"F40.wireOp",EDGE,"E67")])]});
            var Q1;
            Q1=makeQuery(id+"F41.opExtrude","SWEPT_EDGE",EDGE,{"disambiguationData":[OSD([sQuery(id+"F40.wireOp",EDGE,"E63"),sQuery(id+"F40.wireOp",EDGE,"E68")])]});
            var Q2;
            Q2=makeQuery(id+"F41.opExtrude","SWEPT_EDGE",EDGE,{"disambiguationData":[OSD([sQuery(id+"F40.wireOp",EDGE,"E64"),sQuery(id+"F40.wireOp",EDGE,"E65")])]});
            fillet(context, id + "F42", {"entities" : qUnion([Q0, Q1, Q2]), "radius" : 8 * mm, "tangentPropagation" : true, "allowEdgeOverflow" : false});
        }
        {
            var Q0;
            Q0=makeQuery(id+"F41.opExtrude","SWEPT_EDGE",EDGE,{"disambiguationData":[OSD([sQuery(id+"F40.wireOp",EDGE,"E63"),sQuery(id+"F40.wireOp",EDGE,"E64")])]});
            var Q1;
            Q1=makeQuery(id+"F41.opExtrude","SWEPT_EDGE",EDGE,{"disambiguationData":[OSD([sQuery(id+"F40.wireOp",EDGE,"E67"),sQuery(id+"F40.wireOp",EDGE,"E68")])]});
            fillet(context, id + "F43", {"entities" : qUnion([Q0, Q1]), "radius" : 12 * mm, "tangentPropagation" : true, "allowEdgeOverflow" : false});
        }
        {
            var Q0;
            Q0=makeQuery(id+"F41.opExtrude","CAP_FACE",FACE,{"disambiguationData":[OSD([sQuery(id+"F40.wireOp",EDGE,"E63"),sQuery(id+"F40.wireOp",EDGE,"E64"),sQuery(id+"F40.wireOp",EDGE,"E65"),sQuery(id+"F40.wireOp",EDGE,"E66"),sQuery(id+"F40.wireOp",EDGE,"E67"),sQuery(id+"F40.wireOp",EDGE,"E68")])],"isStart":false});
            var Q1;
            Q1=makeQuery(id+"F41.opExtrude","CAP_FACE",FACE,{"disambiguationData":[OSD([sQuery(id+"F40.wireOp",EDGE,"E63"),sQuery(id+"F40.wireOp",EDGE,"E64"),sQuery(id+"F40.wireOp",EDGE,"E65"),sQuery(id+"F40.wireOp",EDGE,"E66"),sQuery(id+"F40.wireOp",EDGE,"E67"),sQuery(id+"F40.wireOp",EDGE,"E68")])],"isStart":true});
            chamfer(context, id + "F44", {"entities" : qUnion([Q0, Q1]), "width" : 3 * mm, "tangentPropagation" : true});
        }
        {
            var Q0;
            Q0=makeQuery(id+"F41.opExtrude","CAP_FACE",FACE,{"disambiguationData":[OSD([sQuery(id+"F40.wireOp",EDGE,"E63"),sQuery(id+"F40.wireOp",EDGE,"E64"),sQuery(id+"F40.wireOp",EDGE,"E65"),sQuery(id+"F40.wireOp",EDGE,"E66"),sQuery(id+"F40.wireOp",EDGE,"E67"),sQuery(id+"F40.wireOp",EDGE,"E68")])],"isStart":true});
            var sketch = newSketch(context, id + "F45", { "sketchPlane" : qUnion([Q0])});
            skCircle(sketch, "E69", {"center": v(48.04, -8.53) * mm, "radius": 2.75 * mm});
            skSolve(sketch);
        }
        {
            var Q0;
            Q0=makeQuery(id+"F45.imprint","IMPRINT",FACE,{"disambiguationData":[TD([[makeQuery(id+"F45.imprint","IMPRINT",EDGE,{"derivedFrom":sQuery(id+"F45.wireOp",EDGE,"E69")}),1.0]])]});
            extrude(context, id + "F46", {"entities" : qUnion([Q0]), "operationType" : NewBodyOperationType.REMOVE, "oppositeDirection" : true, "depth" : 1 * mm});
        }
    });
